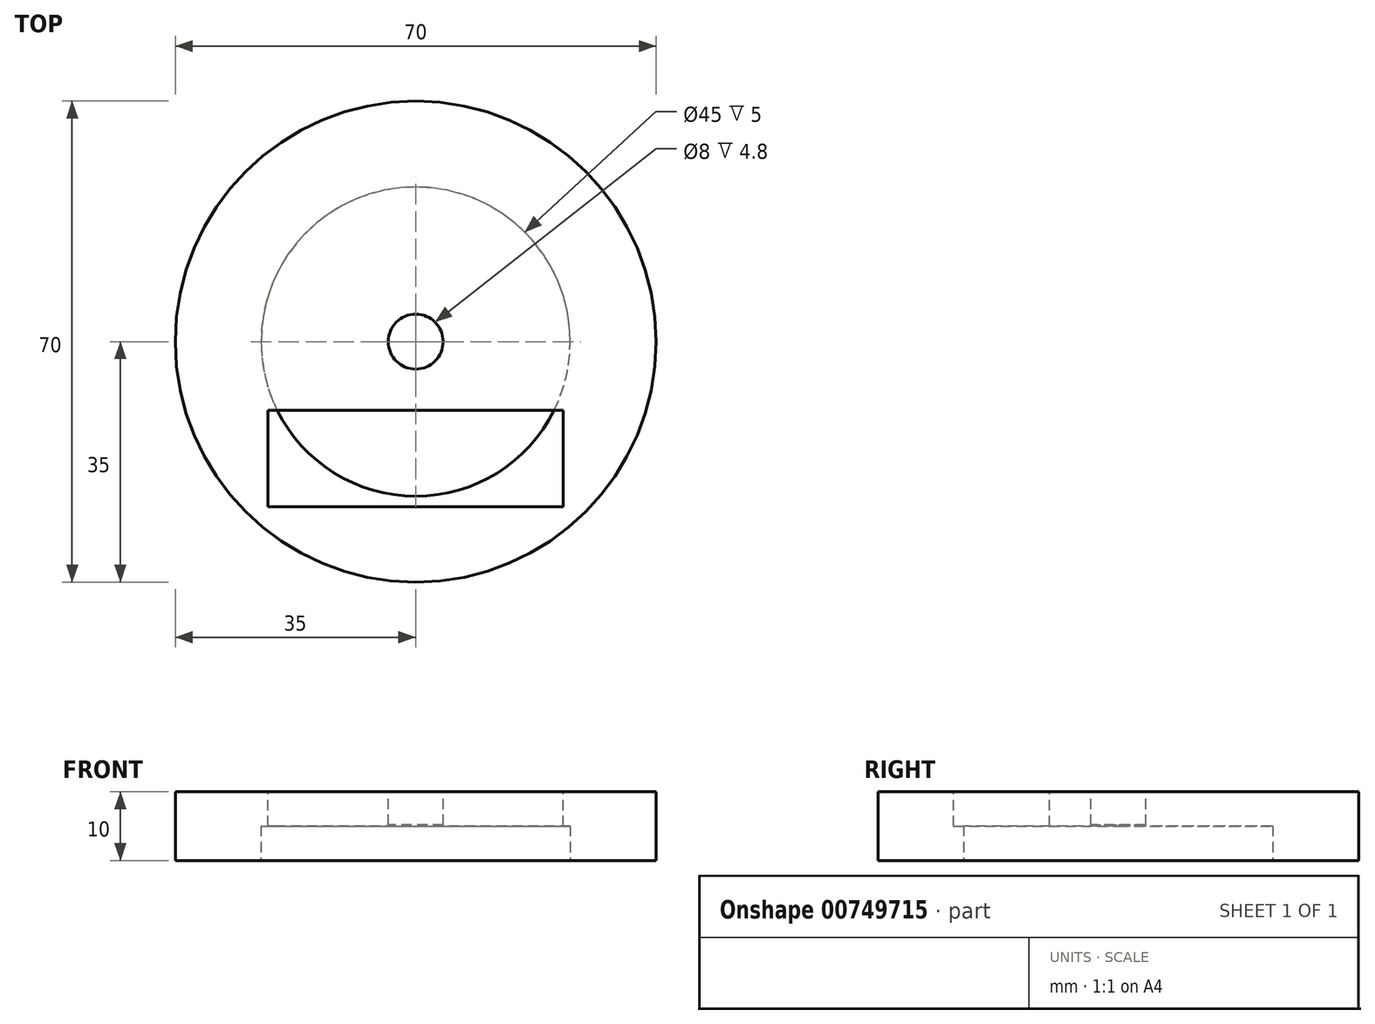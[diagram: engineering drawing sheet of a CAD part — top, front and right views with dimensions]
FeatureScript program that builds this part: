
annotation { "Feature Type Name" : "Feature", "Feature Type Description" : "" }
export const myFeature = defineFeature(function(context is Context, id is Id, definition is map)
    precondition{}
    {
        {
            var Q0;
            Q0=qCreatedBy(makeId("Top.planeOp"),FACE);
            var sketch = newSketch(context, id + "F0", { "sketchPlane" : qUnion([Q0])});
            skCircle(sketch, "E0", {"center": v(0, 0) * mm, "radius": 35 * mm});
            skSolve(sketch);
        }
        {
            var Q0;
            Q0 = qSketchRegion(id + "F0", true);
            extrude(context, id + "F1", {"entities" : qUnion([Q0]), "depth" : 10 * mm, "offsetDistance" : 25 * mm});
        }
        {
            var Q0;
            Q0=makeQuery(id+"F1.opExtrude","CAP_FACE",FACE,{"disambiguationData":[OSD([sQuery(id+"F0.wireOp",EDGE,"E0")])],"isStart":true});
            var sketch = newSketch(context, id + "F2", { "sketchPlane" : qUnion([Q0])});
            skCircle(sketch, "E1", {"center": v(0, 0) * mm, "radius": 22.5 * mm});
            skSolve(sketch);
        }
        {
            var Q0;
            Q0 = qSketchRegion(id + "F2", true);
            extrude(context, id + "F3", {"entities" : qUnion([Q0]), "operationType" : NewBodyOperationType.REMOVE, "oppositeDirection" : true, "depth" : 5 * mm, "offsetDistance" : 25 * mm});
        }
        {
            var Q0;
            Q0=makeQuery(id+"F1.opExtrude","CAP_FACE",FACE,{"disambiguationData":[OSD([sQuery(id+"F0.wireOp",EDGE,"E0")])],"isStart":false});
            var sketch = newSketch(context, id + "F4", { "sketchPlane" : qUnion([Q0])});
            skLineSegment(sketch, "E2.bottom", {"start": v(-21.5, -24) * mm, "end": v(21.5, -24) * mm});
            skLineSegment(sketch, "E2.top", {"start": v(-21.5, -10) * mm, "end": v(21.5, -10) * mm});
            skLineSegment(sketch, "E2.left", {"start": v(-21.5, -24) * mm, "end": v(-21.5, -10) * mm});
            skLineSegment(sketch, "E2.right", {"start": v(21.5, -24) * mm, "end": v(21.5, -10) * mm});
            skPoint(sketch, "E2.middle", {"position": v(0, -17) * mm});
            skSolve(sketch);
        }
        {
            var Q0;
            Q0 = qSketchRegion(id + "F4", true);
            extrude(context, id + "F5", {"entities" : qUnion([Q0]), "operationType" : NewBodyOperationType.REMOVE, "oppositeDirection" : true, "depth" : 5 * mm, "offsetDistance" : 25 * mm});
        }
        {
            var Q0;
            Q0=makeQuery(id+"F1.opExtrude","CAP_FACE",FACE,{"disambiguationData":[OSD([sQuery(id+"F0.wireOp",EDGE,"E0")])],"isStart":false});
            var sketch = newSketch(context, id + "F6", { "sketchPlane" : qUnion([Q0])});
            skCircle(sketch, "E3", {"center": v(0, 0) * mm, "radius": 4 * mm});
            skSolve(sketch);
        }
        {
            var Q0;
            Q0 = qSketchRegion(id + "F6", true);
            extrude(context, id + "F7", {"entities" : qUnion([Q0]), "operationType" : NewBodyOperationType.REMOVE, "oppositeDirection" : true, "depth" : 4.8 * mm, "offsetDistance" : 25 * mm});
        }
    });
